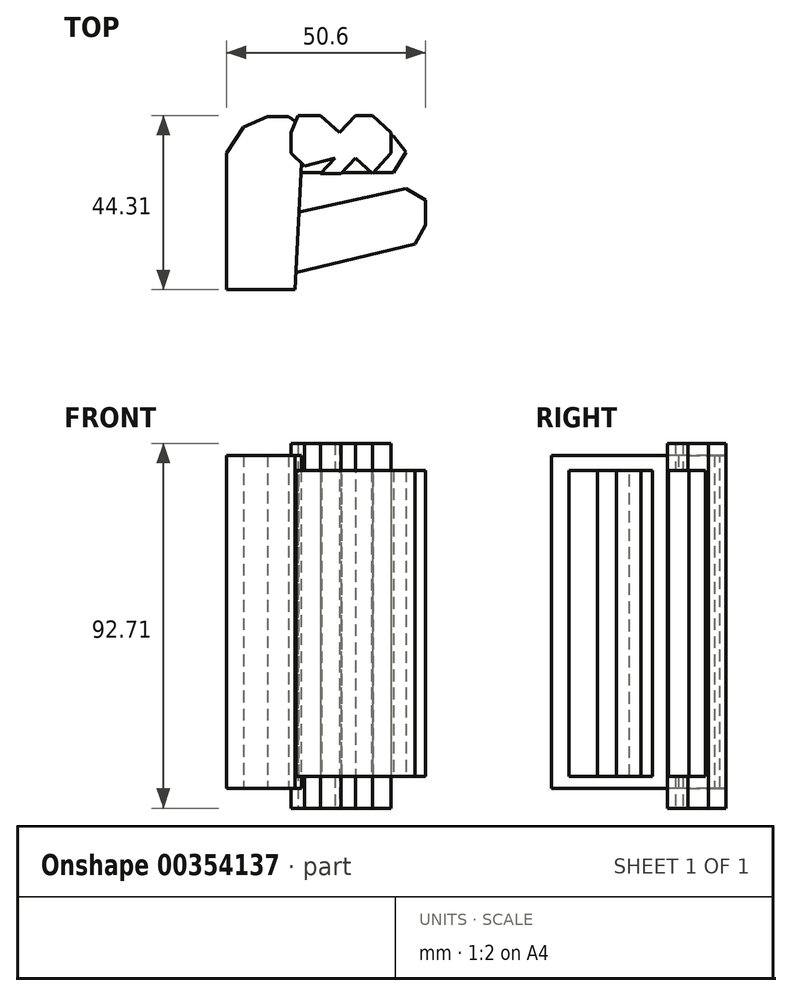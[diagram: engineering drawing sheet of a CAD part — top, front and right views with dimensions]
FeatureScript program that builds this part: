
annotation { "Feature Type Name" : "Feature", "Feature Type Description" : "" }
export const myFeature = defineFeature(function(context is Context, id is Id, definition is map)
    precondition{}
    {
        {
            var Q0;
            Q0=qCreatedBy(makeId("Top.planeOp"),FACE);
            var sketch = newSketch(context, id + "F0", { "sketchPlane" : qUnion([Q0])});
            skLineSegment(sketch, "E0", {"start": v(34.98, -16.47) * mm, "end": v(17.49, -16.47) * mm});
            skLineSegment(sketch, "E1", {"start": v(17.49, -16.47) * mm, "end": v(17.49, 18.22) * mm});
            skLineSegment(sketch, "E2", {"start": v(17.49, 18.22) * mm, "end": v(21.86, 24.92) * mm});
            skLineSegment(sketch, "E3", {"start": v(21.86, 24.92) * mm, "end": v(27.98, 27.54) * mm});
            skLineSegment(sketch, "E4", {"start": v(27.98, 27.54) * mm, "end": v(33.23, 27.54) * mm});
            skLineSegment(sketch, "E5", {"start": v(33.23, 27.54) * mm, "end": v(37.02, 24.92) * mm});
            skLineSegment(sketch, "E6", {"start": v(37.02, 24.92) * mm, "end": v(34.98, -16.47) * mm});
            skSolve(sketch);
        }
        {
            var Q0;
            Q0 = qSketchRegion(id + "F0", true);
            extrude(context, id + "F1", {"entities" : qUnion([Q0]), "depth" : 84.58 * mm});
        }
        {
            var Q0;
            Q0=qCreatedBy(makeId("Top.planeOp"),FACE);
            var sketch = newSketch(context, id + "F2", { "sketchPlane" : qUnion([Q0])});
            skLineSegment(sketch, "E7", {"start": v(20.58, 0) * mm, "end": v(63.14, 9.18) * mm});
            skLineSegment(sketch, "E8", {"start": v(63.14, 9.18) * mm, "end": v(68.1, 6.27) * mm});
            skLineSegment(sketch, "E9", {"start": v(68.1, 6.27) * mm, "end": v(68.1, 0) * mm});
            skLineSegment(sketch, "E10", {"start": v(68.1, 0) * mm, "end": v(65.47, -4.8) * mm});
            skLineSegment(sketch, "E11", {"start": v(65.47, -4.8) * mm, "end": v(22.92, -15.01) * mm});
            skLineSegment(sketch, "E12", {"start": v(22.92, -15.01) * mm, "end": v(20.58, 0) * mm});
            skLineSegment(sketch, "E13", {"start": v(37.2, 22.59) * mm, "end": v(59.93, 22.59) * mm});
            skLineSegment(sketch, "E14", {"start": v(59.93, 22.59) * mm, "end": v(63.14, 18.5) * mm});
            skLineSegment(sketch, "E15", {"start": v(63.14, 18.5) * mm, "end": v(59.93, 13.26) * mm});
            skLineSegment(sketch, "E16", {"start": v(59.93, 13.26) * mm, "end": v(22.92, 13.26) * mm});
            skLineSegment(sketch, "E17", {"start": v(22.92, 13.26) * mm, "end": v(22.92, 22.59) * mm});
            skLineSegment(sketch, "E18", {"start": v(22.92, 22.59) * mm, "end": v(37.2, 22.59) * mm});
            skSolve(sketch);
        }
        {
            var Q0;
            Q0 = qSketchRegion(id + "F2", true);
            extrude(context, id + "F3", {"entities" : qUnion([Q0]), "operationType" : NewBodyOperationType.ADD, "depth" : 80.77 * mm, "hasSecondDirection" : true, "secondDirectionOppositeDirection" : false, "secondDirectionDepth" : 3.05 * mm});
        }
        {
            var Q0;
            Q0=qCreatedBy(makeId("Top.planeOp"),FACE);
            var sketch = newSketch(context, id + "F4", { "sketchPlane" : qUnion([Q0])});
            skLineSegment(sketch, "E19", {"start": v(37.4, 15.01) * mm, "end": v(33.9, 18.22) * mm});
            skLineSegment(sketch, "E20", {"start": v(33.9, 18.22) * mm, "end": v(33.9, 23.46) * mm});
            skLineSegment(sketch, "E21", {"start": v(33.9, 23.46) * mm, "end": v(35.64, 27.84) * mm});
            skPoint(sketch, "E21.endSnap0", {"position": v(35.64, 16.61) * mm});
            skLineSegment(sketch, "E22", {"start": v(35.64, 27.84) * mm, "end": v(41.47, 27.84) * mm});
            skLineSegment(sketch, "E23", {"start": v(41.47, 27.84) * mm, "end": v(46.24, 23.46) * mm});
            skLineSegment(sketch, "E24", {"start": v(46.24, 23.46) * mm, "end": v(50.25, 27.84) * mm});
            skLineSegment(sketch, "E25", {"start": v(50.25, 27.84) * mm, "end": v(54.59, 27.84) * mm});
            skLineSegment(sketch, "E26", {"start": v(54.59, 27.84) * mm, "end": v(59.36, 23.46) * mm});
            skLineSegment(sketch, "E27", {"start": v(59.36, 23.46) * mm, "end": v(59.36, 18.22) * mm});
            skLineSegment(sketch, "E28", {"start": v(59.36, 18.22) * mm, "end": v(54.59, 13.01) * mm});
            skLineSegment(sketch, "E29", {"start": v(54.59, 13.01) * mm, "end": v(50.25, 17) * mm});
            skLineSegment(sketch, "E30", {"start": v(50.25, 17) * mm, "end": v(46.6, 13.01) * mm});
            skLineSegment(sketch, "E31", {"start": v(46.6, 13.01) * mm, "end": v(41.47, 13.01) * mm});
            skLineSegment(sketch, "E32", {"start": v(41.47, 13.01) * mm, "end": v(45.12, 17) * mm});
            skLineSegment(sketch, "E33", {"start": v(45.12, 17) * mm, "end": v(37.4, 15.01) * mm});
            skSolve(sketch);
        }
        {
            var Q0;
            Q0 = qSketchRegion(id + "F4", true);
            extrude(context, id + "F5", {"entities" : qUnion([Q0]), "operationType" : NewBodyOperationType.ADD, "depth" : 87.63 * mm, "hasSecondDirection" : true, "secondDirectionOppositeDirection" : true, "secondDirectionDepth" : 5.08 * mm});
        }
    });
